# Revit family: Quinta Ace 135kW LOD 3
name_source: partatom
category: Mechanical Equipment
units: mm (PartAtom-declared; Revit-internal decimal feet)

## family parameters
Always vertical = Yes
Cut with Voids When Loaded = No
OmniClass Number = 23.75.10.11.14.14
OmniClass Title = Condensing Boilers
Part Type = Normal
Room Calculation Point = No
Round Connector Dimension = Use Radius
Shared = No
Work Plane-Based = No

## types (1)
- 135kW
    6 Monthly = 06-02
    Access Clearance Bottom = 300 mm  [stored 0.984252 ft]
    Access Clearance Front = 1000 mm
    Access Clearance Left = 30 mm
    Access Clearance Rear = 0 mm  [stored 0 ft]
    Access Clearance Right = 30 mm
    Access Clearance Top = 500 mm
    Additional Technical Details = Not Available
    Air Inlet Connection Size = 150 mm
    Annually = 06-02
    BMS Links = Yes
    Bespoke Timeframe = 0
    Building Regulations Seasonal Efficiency = 97.18 %
    Burner Control Type = Modulating
    CE Mark = 0063CQ3781
    Colour = RAL 9016
    Condensate Drain Size = 32 mm  [stored 0.104987 ft]
    Condensate Drain Type = Plain
    Configuration = Single boiler
    Control Type = 0 - 10V, Open Therm, Volt free enable, Direct boiler weather compensating control systems available from Remeha as optional extra's.
    Daily = 0
    Default Elevation = 0 mm  [stored 0 ft]
    Drain Connection Size = 0 mm  [stored 0 ft]
    ErP Energy Label = 0
    ErP Rated Efficiency at Full Load = 93.60 %
    ErP Rated Efficiency at Part Load = 98.02 %
    ErP Seasonal Efficiency = 0 %
    Expected Life = 15
    External Material = Steel
    Features = The Quinta Ace range is a market leading series of versatile, wall hung condensing boilers designed for space heating and hot water production
    Finish = High Polish Gardner 60 GRAD 91EH
    Flow and Return Connection Size = 32 mm  [stored 0.104987 ft]
    Flow and Return Connection Type = Threaded
    Flue Connection size = 100 mm  [stored 0.328084 ft]
    Flue or Air Intake Classification = B23p, C13, C33, C53
    Frequency = 50 Hz
    Fuel Connection Size = 25 mm  [stored 0.082021 ft]
    Fuel Connection Type = Threaded
    Full Load Current = 0 A
    Fuse Rating = 6 A
    Gas Consumption rate = 13.9 m3/h
    Gross Weight = 164.00 kg
    Heat Exchanger Material = Aluminium
    Heater Operation = Condensing
    Hydraulic Resistance at 11C temperature differential = 0.0
    Hydraulic Resistance at 20C temperature differential = 0.2
    IK Rating = 0
    IP Rating = X1B
    IfcExportAs = IfcBoilerType
    IfcExportType = NOTDEFINED
    Interlocks = Yes
    Maintenance Required 0 to 300hrs = 0
    Maintenance Required 1001 to 2000hrs = 0
    Maintenance Required 2001 to 4000hrs = 0
    Maintenance Required 301 to 600hrs = 0
    Maintenance Required 4001 to 8000hrs = 0
    Maintenance Required 601 to 1000hrs = 0
    Maintenance Required 8001 to 12000hrs = 0
    Manufacturer = Remeha Commercial
    Manufacturer Website = https://www.remeha.co.uk
    Maximum Gas Inlet Pressure = 0.0 bar
    Maximum Oil Inlet Pressure = 0.0 bar
    Maximum Operating Pressure = 4.0 bar
    Maximum Power Consumption = 199 W
    Minimum Flow Rate at 11C temperature differential = 0.0 L/s
    Minimum Flow Rate at 20C temperature differential = 1.5 L/s
    Minimum Gas Inlet Pressure = 0.0 bar
    Minimum Oil Inlet Pressure = 0.0 bar
    Minimum Operating Pressure = 0.8 bar
    Minimum Power Consumption = 5 W
    Monthly = 0
    Mounting = Wall Mounted
    NOx Emissions = 24 mg/kWh
    Nominal Gas Inlet Pressure = 0.0 bar
    Nominal Oil Inlet Pressure = 0.0 bar
    Oil Consumption rate = 0
    Operation and Maintenance Manual = https://www.remeha.co.uk
    Optional Fuel = Gas - LPG
    Overall Height = 1045 mm  [stored 3.42848 ft]
    Overall Length = 602 mm
    Overall Width = 600 mm
    Primary Fuel = Gas - NG
    Product Literature = https://www.remeha.co.uk
    Product Model Number = 7780036
    Product Range = Quinta Ace 135
    Quarterly = 0
    Rated Criteria = 50/30
    Rated Output = 136100 W
    Reference Standard = EU/2016/426 GAR, EN 15502-1, EN 15502-2
    Safety Valve Connection Size = 0 mm  [stored 0 ft]
    Shape = Rectangular (Vertical)
    Shipping Weight = 0.00 kg
    Sound Pressure Level = 59.5 dBA
    Starting Current = 0 A
    Supply Phase = 1
    Turndown Ratio = 5:1
    Type = Space heating
    Uniclass2015 = Pr_60_60_08
    Voltage = 230 V
    Water Content = 17.0 L
    Water Treatment Required = Yes
    Weekly = 0

note: source unit labels omitted for Hydraulic Resistance at 11C temperature differential, Hydraulic Resistance at 20C temperature differential — the stored unit's dimension contradicts the parameter name (converter mislabeling)

note: [stored X ft] marks values corroborated as IEEE doubles in the binary element streams (Revit-internal decimal feet)

## geometry (parser evidence)
native form markers: Blend x13, Sweep x3
no freeform markers — native parametric forms only
